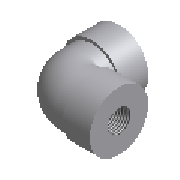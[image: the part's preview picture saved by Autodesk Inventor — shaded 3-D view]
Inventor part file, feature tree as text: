
AUTODESK INVENTOR PART (.ipt)
format: ipt  version: 2023 (Build 270158000, 158)  size: 268,288 bytes
history: native  units: mm (DEFAULTED — no unit token found)
features: other x6, revolve x4, sketch x2, sweep x2, plane x1
ambient origin geometry x8: Origin, YZ Plane, XZ Plane, XY Plane, X Axis, Y Axis, Z Axis, Center Point
bodies: Solid1 (feature_tree)
feature tree (15):
  sketch  "Sketch1"  dims[d0=18.320766mm d1=38.1mm d2=0.312398mm d3=0.312398mm]
  plane  "Work Plane1"
  sketch  "Sketch2"  dims[d4=18.320766mm d5=38.1mm d6=13.55598mm d7=26.1112mm d8=13.55598mm d9=26.1112mm d10=0.0mm d11=9.9822mm d12=9.9822mm d13=17.145mm d14=0.0mm d101=90.0deg d102=90.0deg d105=25.4mm d106=0.0mm d107=25.4mm d108=0.0mm d15=33.274mm d16=16.637mm d17=33.274mm d18=16.637mm d19=34.29mm d20=34.29mm d21=9.9822mm d116=90.0deg d117=90.0deg d22=13.055641mm d23=0.0mm d122=0.0mm d123=0.0mm]
  sweep  "Sweep1"
  revolve  "Revolve1"  [1 undecoded]
  revolve  "Revolve2"  [1 undecoded]
  revolve  "Revolve3"  [1 undecoded]
  revolve  "Revolve4"  [1 undecoded]
  sweep  "Sweep2"
  other  "Work Axis1"
  other  "Work Point1"
  other  "Work Point2"
  other  "Work Axis2"
  other  "Work Point3"
  other  "Work Point4"
note: 4 required parameter values undecoded (feature->parameter linkage not recoverable at this tier; creation-order binding heuristic only, values carry confidence <= 0.55)
